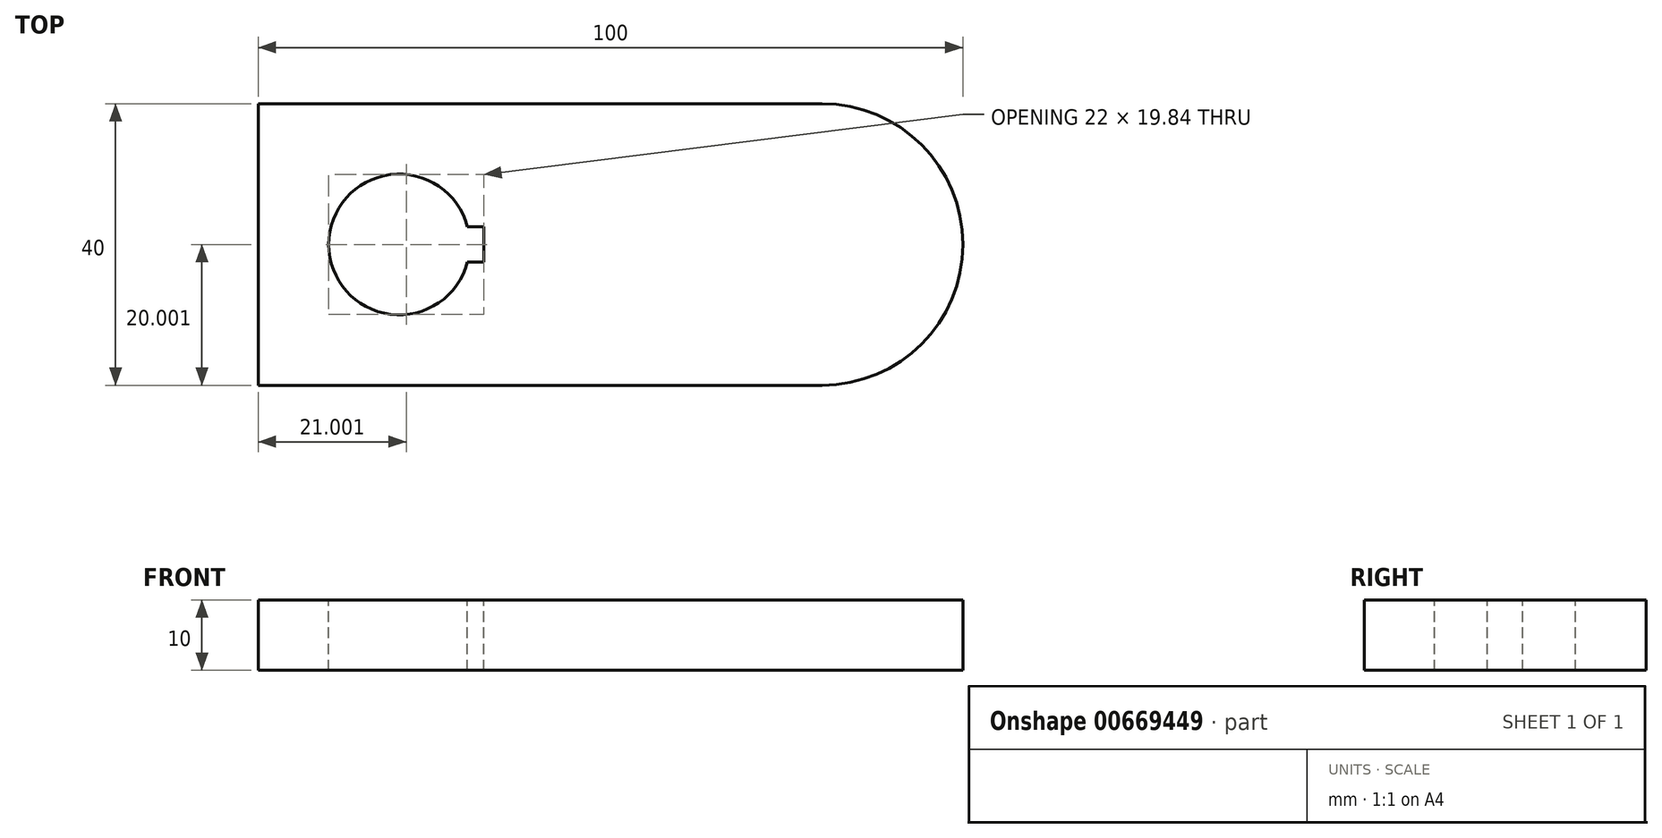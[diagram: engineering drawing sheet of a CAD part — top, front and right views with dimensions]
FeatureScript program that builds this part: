
annotation { "Feature Type Name" : "Feature", "Feature Type Description" : "" }
export const myFeature = defineFeature(function(context is Context, id is Id, definition is map)
    precondition{}
    {
        {
            var Q0;
            Q0=qCreatedBy(makeId("Top.planeOp"),FACE);
            var sketch = newSketch(context, id + "F0", { "sketchPlane" : qUnion([Q0])});
            skLineSegment(sketch, "E0.bottom", {"start": v(-69.42, 52.37) * mm, "end": v(10.58, 52.37) * mm});
            skLineSegment(sketch, "E0.top", {"start": v(-69.42, 12.37) * mm, "end": v(10.58, 12.37) * mm});
            skLineSegment(sketch, "E0.left", {"start": v(-69.42, 52.37) * mm, "end": v(-69.42, 12.37) * mm});
            skArc(sketch, "E1", {"start": v(10.58, 12.37) * mm, "mid": v(30.58, 32.37) * mm, "end": v(10.58, 52.37) * mm});
            skArc(sketch, "E2", {"start": v(-39.74, 34.87) * mm, "mid": v(-59.42, 32.37) * mm, "end": v(-39.74, 29.87) * mm});
            skLineSegment(sketch, "E3.bottom", {"start": v(-37.42, 29.87) * mm, "end": v(-39.74, 29.87) * mm});
            skLineSegment(sketch, "E3.top", {"start": v(-37.42, 34.87) * mm, "end": v(-39.74, 34.87) * mm});
            skLineSegment(sketch, "E3.left", {"start": v(-37.42, 29.87) * mm, "end": v(-37.42, 34.87) * mm});
            skPoint(sketch, "E3.middle", {"position": v(-39.42, 32.37) * mm});
            skPoint(sketch, "E3.right.end.orphan", {"position": v(-41.42, 34.87) * mm});
            skPoint(sketch, "E4.orphan", {"position": v(-41.42, 29.87) * mm});
            skSolve(sketch);
        }
        {
            var Q0;
            Q0=makeQuery(id+"F0.imprint","IMPRINT",FACE,{"disambiguationData":[TD([[makeQuery(id+"F0.imprint","IMPRINT",EDGE,{"derivedFrom":sQuery(id+"F0.wireOp",EDGE,"E0.bottom")}),-1.0]])]});
            extrude(context, id + "F1", {"entities" : qUnion([Q0]), "oppositeDirection" : true, "depth" : 10 * mm, "offsetDistance" : 25 * mm});
        }
    });
